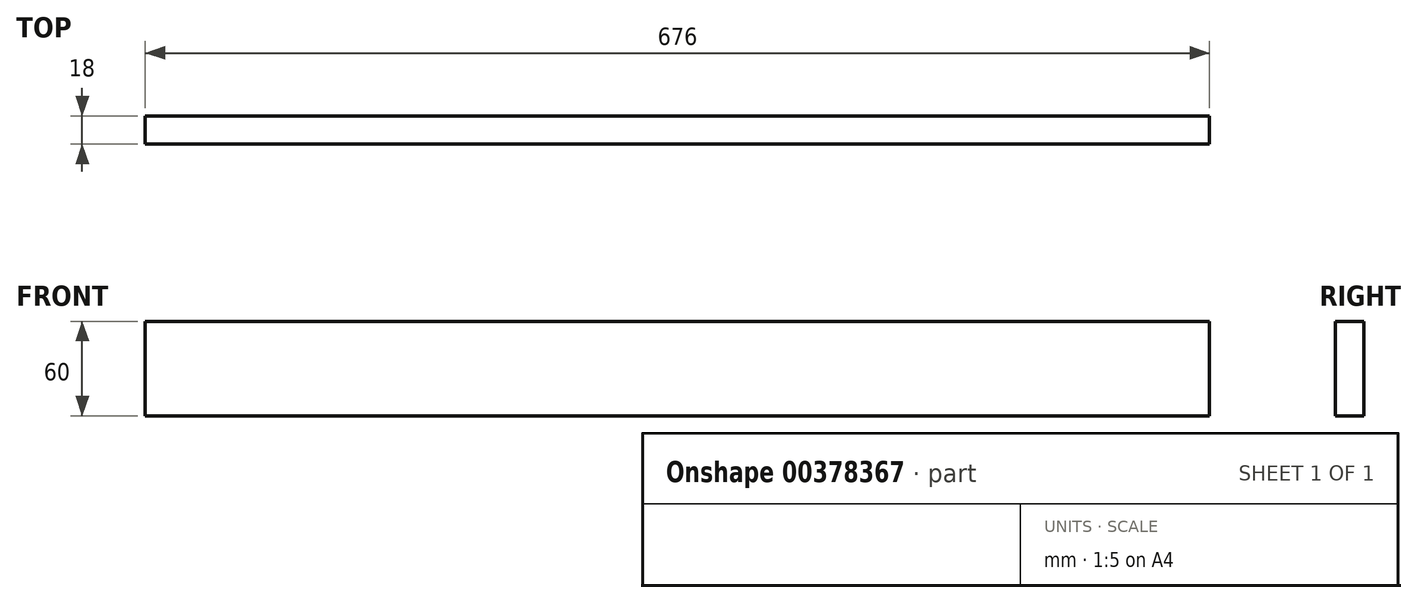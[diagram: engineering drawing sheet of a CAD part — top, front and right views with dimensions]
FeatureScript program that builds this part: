
annotation { "Feature Type Name" : "Feature", "Feature Type Description" : "" }
export const myFeature = defineFeature(function(context is Context, id is Id, definition is map)
    precondition{}
    {
        {
            var Q0;
            Q0=qCreatedBy(makeId("Right.planeOp"),FACE);
            var sketch = newSketch(context, id + "F0", { "sketchPlane" : qUnion([Q0])});
            skLineSegment(sketch, "E0.bottom", {"start": v(9, 30) * mm, "end": v(-9, 30) * mm});
            skLineSegment(sketch, "E0.top", {"start": v(9, -30) * mm, "end": v(-9, -30) * mm});
            skLineSegment(sketch, "E0.left", {"start": v(9, 30) * mm, "end": v(9, -30) * mm});
            skLineSegment(sketch, "E0.right", {"start": v(-9, 30) * mm, "end": v(-9, -30) * mm});
            skPoint(sketch, "E0.middle", {"position": v(0, 0) * mm});
            skSolve(sketch);
        }
        {
            var Q0;
            Q0=qSketchRegion(id+"F0",true);
            extrude(context, id + "F1", {"entities" : qUnion([Q0]), "depth" : 676 * mm});
        }
    });
